# Revit family: RN 90082 Optifitt-Serra-Rohrnippel
name_source: partatom
category: Rohrformteile
units: mm (PartAtom-declared; Revit-internal decimal feet)

## family parameters
Arbeitsebenenbasiert = Nein
Beim Laden mit Abzugskörper schneiden = Nein
Bemaßung runder Anschluss = Durchmesser verwenden
Gemeinsam genutzt = Nein
Immer vertikal = Ja
Teiletyp = Nicht definiert

## types (8) — shared parameters
1.010.00.2 Blattnummer der Richtlinie = 29
1.010.00.3 Ausgabedatum (Monat) der Richtlinie = 201308
1.010.00.4 Herstellername = R. Nussbaum AG
1.010.00.5 Revisionsdatum der Datei = 20190521
1.010.00.6 Webadresse des Herstellers = http://www.nussbaum.ch
1.100.00.4 Produktbezeichnung = Versorgung
1.110.00.2 Index = 3
1.110.00.4 Produktbezeichnung = Optifitt-Serra
1.960/3L.00.8 Link (URL) = https://www.nussbaum.ch
29.700.00.4 Produktname = Optifitt-Serra-Rohrnippel
29.700.00.5 Produktkennung = 2
29.700.00.6 Querschnittsform = 1
29.700.00.7 Nennweitensystem = DN
29.700.00.8 Nenndrucksystem = PN
29.710.02.4 Nenndruck = 16
29.710.02.5 max. zul. Überdruck [hPa] = 1600
29.710.02.7 max. zul. Dauer-Betriebsdruck [hPa] = 1600
29.710.02.9 max. zul. Dauer-Betriebstemperatur [°C] = 90
Connector Visibility = Nein
EnclosingSpace Visibility = Nein
Hersteller = R. Nussbaum AG
URL = https://www.nussbaum.ch

## per-type parameters (varying)
- DN=65: 1.800.00.3 TGA-Nummer=01900300000000000000000000000000000000000000000019000000000000000075; 1.800.00.4 Kommentarfeld=90082.10, Optifitt-Serra-Rohrnippel, DN=65, L=100, R=2½; 1.810.00.3 Hersteller-Bestellnummer=90082.1; 1.810.00.4 DATANORM-Nummer=90082.1; 1.810.00.5 StLB-Nummer=214.238; 1.810.00.6 GTIN-Nummer=7612945681171; 29.710.02.10 Formstück-Gewicht [kg]=0.493; 29.710.02.3 Benennung=Optifitt-Serra-Rohrnippel, DN=65, L=100, R=2½; CONNECTOR0_DIAMETER_dX_0r=65 mm; CONNECTOR0_dX_01=27 mm  [stored 0.0885827 ft]; CONNECTOR0_ref_dX=27 mm  [stored 0.0885827 ft]; CONNECTOR1_DIAMETER_dX_0r=65 mm; CONNECTOR1_dX_00=73 mm; CONNECTOR1_dX_01=100 mm  [stored 0.328084 ft]; CONNECTOR1_ref_dX=73 mm; CONNECTOR1_ref_dX2=100 mm  [stored 0.328084 ft]; Modell=90082.1; R. Nussbaum AG 90082.04 de Visibility=Nein; R. Nussbaum AG 90082.05 de Visibility=Nein; R. Nussbaum AG 90082.06 de Visibility=Nein; R. Nussbaum AG 90082.07 de Visibility=Nein; R. Nussbaum AG 90082.08 de Visibility=Nein; R. Nussbaum AG 90082.09 de Visibility=Nein; R. Nussbaum AG 90082.10 de Visibility=Ja; R. Nussbaum AG 90082.11 de Visibility=Nein; Typenkommentare=Optifitt-Serra-Rohrnippel  DN=65
- DN=80: 1.800.00.3 TGA-Nummer=01900300000000000000000000000000000000000000000019000000000000000064; 1.800.00.4 Kommentarfeld=90082.11, Optifitt-Serra-Rohrnippel, DN=80, L=120, R=3; 1.810.00.3 Hersteller-Bestellnummer=90082.11; 1.810.00.4 DATANORM-Nummer=90082.11; 1.810.00.6 GTIN-Nummer=7612945681188; 29.710.02.10 Formstück-Gewicht [kg]=0.995; 29.710.02.3 Benennung=Optifitt-Serra-Rohrnippel, DN=80, L=120, R=3; CONNECTOR0_DIAMETER_dX_0r=80 mm; CONNECTOR0_dX_01=30 mm; CONNECTOR0_ref_dX=30 mm; CONNECTOR1_DIAMETER_dX_0r=80 mm; CONNECTOR1_dX_00=90 mm; CONNECTOR1_dX_01=120 mm; CONNECTOR1_ref_dX=90 mm; CONNECTOR1_ref_dX2=120 mm; Modell=90082.11; R. Nussbaum AG 90082.04 de Visibility=Nein; R. Nussbaum AG 90082.05 de Visibility=Nein; R. Nussbaum AG 90082.06 de Visibility=Nein; R. Nussbaum AG 90082.07 de Visibility=Nein; R. Nussbaum AG 90082.08 de Visibility=Nein; R. Nussbaum AG 90082.09 de Visibility=Nein; R. Nussbaum AG 90082.10 de Visibility=Nein; R. Nussbaum AG 90082.11 de Visibility=Ja; Typenkommentare=Optifitt-Serra-Rohrnippel  DN=80
- DN=50: 1.800.00.3 TGA-Nummer=01900300000000000000000000000000000000000000000019000000000000000063; 1.800.00.4 Kommentarfeld=90082.09, Optifitt-Serra-Rohrnippel, DN=50, L=100, R=2; 1.810.00.3 Hersteller-Bestellnummer=90082.09; 1.810.00.4 DATANORM-Nummer=90082.09; 1.810.00.5 StLB-Nummer=214.237; 1.810.00.6 GTIN-Nummer=7612945681164; 29.710.02.10 Formstück-Gewicht [kg]=0.386; 29.710.02.3 Benennung=Optifitt-Serra-Rohrnippel, DN=50, L=100, R=2; CONNECTOR0_DIAMETER_dX_0r=50 mm; CONNECTOR0_dX_01=24 mm; CONNECTOR0_ref_dX=24 mm; CONNECTOR1_DIAMETER_dX_0r=50 mm; CONNECTOR1_dX_00=76 mm; CONNECTOR1_dX_01=100 mm  [stored 0.328084 ft]; CONNECTOR1_ref_dX=76 mm; CONNECTOR1_ref_dX2=100 mm  [stored 0.328084 ft]; Modell=90082.09; R. Nussbaum AG 90082.04 de Visibility=Nein; R. Nussbaum AG 90082.05 de Visibility=Nein; R. Nussbaum AG 90082.06 de Visibility=Nein; R. Nussbaum AG 90082.07 de Visibility=Nein; R. Nussbaum AG 90082.08 de Visibility=Nein; R. Nussbaum AG 90082.09 de Visibility=Ja; R. Nussbaum AG 90082.10 de Visibility=Nein; R. Nussbaum AG 90082.11 de Visibility=Nein; Typenkommentare=Optifitt-Serra-Rohrnippel  DN=50
- DN=40: 1.800.00.3 TGA-Nummer=01900300000000000000000000000000000000000000000019000000000000000062; 1.800.00.4 Kommentarfeld=90082.08, Optifitt-Serra-Rohrnippel, DN=40, L=100, R=1½; 1.810.00.3 Hersteller-Bestellnummer=90082.08; 1.810.00.4 DATANORM-Nummer=90082.08; 1.810.00.5 StLB-Nummer=214.236; 1.810.00.6 GTIN-Nummer=7612945681157; 29.710.02.10 Formstück-Gewicht [kg]=0.262; 29.710.02.3 Benennung=Optifitt-Serra-Rohrnippel, DN=40, L=100, R=1½; CONNECTOR0_DIAMETER_dX_0r=40 mm; CONNECTOR0_dX_01=19 mm; CONNECTOR0_ref_dX=19 mm; CONNECTOR1_DIAMETER_dX_0r=40 mm; CONNECTOR1_dX_00=61 mm; CONNECTOR1_dX_01=80 mm; CONNECTOR1_ref_dX=61 mm; CONNECTOR1_ref_dX2=80 mm; Modell=90082.08; R. Nussbaum AG 90082.04 de Visibility=Nein; R. Nussbaum AG 90082.05 de Visibility=Nein; R. Nussbaum AG 90082.06 de Visibility=Nein; R. Nussbaum AG 90082.07 de Visibility=Nein; R. Nussbaum AG 90082.08 de Visibility=Ja; R. Nussbaum AG 90082.09 de Visibility=Nein; R. Nussbaum AG 90082.10 de Visibility=Nein; R. Nussbaum AG 90082.11 de Visibility=Nein; Typenkommentare=Optifitt-Serra-Rohrnippel  DN=40
- DN=32: 1.800.00.3 TGA-Nummer=01900300000000000000000000000000000000000000000019000000000000000061; 1.800.00.4 Kommentarfeld=90082.07, Optifitt-Serra-Rohrnippel, DN=32, L=80, R=1¼; 1.810.00.3 Hersteller-Bestellnummer=90082.07; 1.810.00.4 DATANORM-Nummer=90082.07; 1.810.00.5 StLB-Nummer=214.235; 1.810.00.6 GTIN-Nummer=7612945681140; 29.710.02.10 Formstück-Gewicht [kg]=0.185; 29.710.02.3 Benennung=Optifitt-Serra-Rohrnippel, DN=32, L=80, R=1¼; CONNECTOR0_DIAMETER_dX_0r=32 mm; CONNECTOR0_dX_01=19 mm; CONNECTOR0_ref_dX=19 mm; CONNECTOR1_DIAMETER_dX_0r=32 mm; CONNECTOR1_dX_00=61 mm; CONNECTOR1_dX_01=80 mm; CONNECTOR1_ref_dX=61 mm; CONNECTOR1_ref_dX2=80 mm; Modell=90082.07; R. Nussbaum AG 90082.04 de Visibility=Nein; R. Nussbaum AG 90082.05 de Visibility=Nein; R. Nussbaum AG 90082.06 de Visibility=Nein; R. Nussbaum AG 90082.07 de Visibility=Ja; R. Nussbaum AG 90082.08 de Visibility=Nein; R. Nussbaum AG 90082.09 de Visibility=Nein; R. Nussbaum AG 90082.10 de Visibility=Nein; R. Nussbaum AG 90082.11 de Visibility=Nein; Typenkommentare=Optifitt-Serra-Rohrnippel  DN=32
- DN=25: 1.800.00.3 TGA-Nummer=01900300000000000000000000000000000000000000000019000000000000000060; 1.800.00.4 Kommentarfeld=90082.06, Optifitt-Serra-Rohrnippel, DN=25, L=80, R=1; 1.810.00.3 Hersteller-Bestellnummer=90082.06; 1.810.00.4 DATANORM-Nummer=90082.06; 1.810.00.5 StLB-Nummer=214.234; 1.810.00.6 GTIN-Nummer=7612945681133; 29.710.02.10 Formstück-Gewicht [kg]=0.156; 29.710.02.3 Benennung=Optifitt-Serra-Rohrnippel, DN=25, L=80, R=1; CONNECTOR0_DIAMETER_dX_0r=25 mm  [stored 0.082021 ft]; CONNECTOR0_dX_01=17 mm; CONNECTOR0_ref_dX=17 mm; CONNECTOR1_DIAMETER_dX_0r=25 mm  [stored 0.082021 ft]; CONNECTOR1_dX_00=63 mm; CONNECTOR1_dX_01=80 mm; CONNECTOR1_ref_dX=63 mm; CONNECTOR1_ref_dX2=80 mm; Modell=90082.06; R. Nussbaum AG 90082.04 de Visibility=Nein; R. Nussbaum AG 90082.05 de Visibility=Nein; R. Nussbaum AG 90082.06 de Visibility=Ja; R. Nussbaum AG 90082.07 de Visibility=Nein; R. Nussbaum AG 90082.08 de Visibility=Nein; R. Nussbaum AG 90082.09 de Visibility=Nein; R. Nussbaum AG 90082.10 de Visibility=Nein; R. Nussbaum AG 90082.11 de Visibility=Nein; Typenkommentare=Optifitt-Serra-Rohrnippel  DN=25
- DN=20: 1.800.00.3 TGA-Nummer=01900300000000000000000000000000000000000000000019000000000000000059; 1.800.00.4 Kommentarfeld=90082.05, Optifitt-Serra-Rohrnippel, DN=20, L=60, R=¾; 1.810.00.3 Hersteller-Bestellnummer=90082.05; 1.810.00.4 DATANORM-Nummer=90082.05; 1.810.00.5 StLB-Nummer=214.233; 1.810.00.6 GTIN-Nummer=7612945681126; 29.710.02.10 Formstück-Gewicht [kg]=0.066; 29.710.02.3 Benennung=Optifitt-Serra-Rohrnippel, DN=20, L=60, R=¾; CONNECTOR0_DIAMETER_dX_0r=20 mm; CONNECTOR0_dX_01=15 mm  [stored 0.0492126 ft]; CONNECTOR0_ref_dX=15 mm  [stored 0.0492126 ft]; CONNECTOR1_DIAMETER_dX_0r=20 mm; CONNECTOR1_dX_00=45 mm; CONNECTOR1_dX_01=60 mm  [stored 0.19685 ft]; CONNECTOR1_ref_dX=45 mm; CONNECTOR1_ref_dX2=60 mm  [stored 0.19685 ft]; Modell=90082.05; R. Nussbaum AG 90082.04 de Visibility=Nein; R. Nussbaum AG 90082.05 de Visibility=Ja; R. Nussbaum AG 90082.06 de Visibility=Nein; R. Nussbaum AG 90082.07 de Visibility=Nein; R. Nussbaum AG 90082.08 de Visibility=Nein; R. Nussbaum AG 90082.09 de Visibility=Nein; R. Nussbaum AG 90082.10 de Visibility=Nein; R. Nussbaum AG 90082.11 de Visibility=Nein; Typenkommentare=Optifitt-Serra-Rohrnippel  DN=20
- DN=15: 1.800.00.3 TGA-Nummer=01900300000000000000000000000000000000000000000019000000000000000058; 1.800.00.4 Kommentarfeld=90082.04, Optifitt-Serra-Rohrnippel, DN=15, L=40, R=½; 1.810.00.3 Hersteller-Bestellnummer=90082.04; 1.810.00.4 DATANORM-Nummer=90082.04; 1.810.00.5 StLB-Nummer=214.232; 1.810.00.6 GTIN-Nummer=7612945681119; 29.710.02.10 Formstück-Gewicht [kg]=0.029; 29.710.02.3 Benennung=Optifitt-Serra-Rohrnippel, DN=15, L=40, R=½; CONNECTOR0_DIAMETER_dX_0r=15 mm  [stored 0.0492126 ft]; CONNECTOR0_dX_01=13 mm; CONNECTOR0_ref_dX=13 mm; CONNECTOR1_DIAMETER_dX_0r=15 mm  [stored 0.0492126 ft]; CONNECTOR1_dX_00=27 mm  [stored 0.0885827 ft]; CONNECTOR1_dX_01=40 mm; CONNECTOR1_ref_dX=27 mm  [stored 0.0885827 ft]; CONNECTOR1_ref_dX2=40 mm; Modell=90082.04; R. Nussbaum AG 90082.04 de Visibility=Ja; R. Nussbaum AG 90082.05 de Visibility=Nein; R. Nussbaum AG 90082.06 de Visibility=Nein; R. Nussbaum AG 90082.07 de Visibility=Nein; R. Nussbaum AG 90082.08 de Visibility=Nein; R. Nussbaum AG 90082.09 de Visibility=Nein; R. Nussbaum AG 90082.10 de Visibility=Nein; R. Nussbaum AG 90082.11 de Visibility=Nein; Typenkommentare=Optifitt-Serra-Rohrnippel  DN=15

note: [stored X ft] marks values corroborated as IEEE doubles in the binary element streams (Revit-internal decimal feet)

## geometry (parser evidence)
native form markers: Sweep x2
no freeform markers — native parametric forms only
